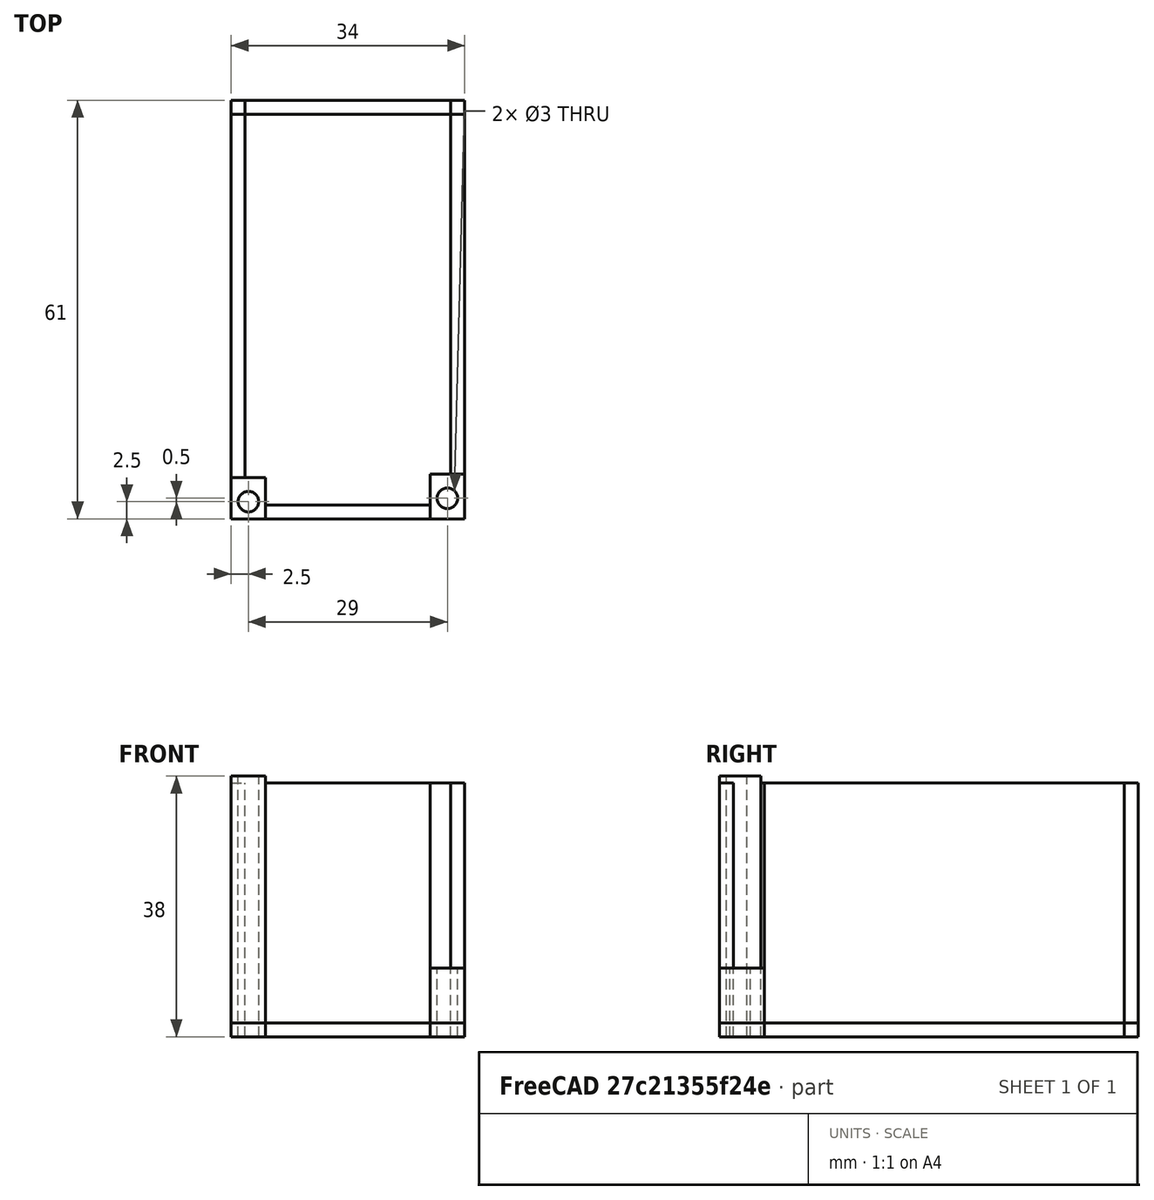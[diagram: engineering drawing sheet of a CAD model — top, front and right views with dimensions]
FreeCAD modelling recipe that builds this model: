
FCSTD DOCUMENT  (FreeCAD 0.16R6700 (Git))
Label: Battery case
License: All rights reserved
LicenseURL: http://en.wikipedia.org/wiki/All_rights_reserved
objects: Part::Box×7, Part::Cylinder×2, Part::Cut×2
note: 11 computed .brp shape members not serialized (recipe doc carries the construction recipe); baked Part::Feature solids carry a one-line shape summary decoded from their .brp

FEATURE [Part::Box] Box  label="Cube"
  Height = 2
  Length = 34
  Width = 61
FEATURE [Part::Box] Box001  label="Cube001"
  Height = 37
  Length = 2
  Placement = pos=(0,6,0) rot=(0,0,1;0rad)
  Width = 55
FEATURE [Part::Box] Box002  label="Cube002"
  Height = 37
  Length = 2
  Placement = pos=(32,6.5,0) rot=(0,0,1;0rad)
  Width = 54.5
FEATURE [Part::Box] Box003  label="Cube003"
  Height = 37
  Length = 34
  Placement = pos=(0,59,0) rot=(0,0,1;0rad)
  Width = 2
FEATURE [Part::Box] Box004  label="Cube004"
  Height = 37
  Length = 24
  Placement = pos=(5,0,0) rot=(0,0,1;0rad)
  Width = 2
FEATURE [Part::Cylinder] Cylinder
  Angle = 360
  Height = 38
  Placement = pos=(2.5,2.5,0) rot=(0,0,1;0rad)
  Radius = 1.5
FEATURE [Part::Box] Box005  label="Cube005"
  Height = 38
  Length = 5
  Width = 6
FEATURE [Part::Box] Box006  label="Cube006"
  Height = 10
  Length = 5
  Placement = pos=(29,0,0) rot=(0,0,1;0rad)
  Width = 6.5
FEATURE [Part::Cylinder] Cylinder001
  Angle = 360
  Height = 10
  Placement = pos=(31.5,3,0) rot=(0,0,1;0rad)
  Radius = 1.5
FEATURE [Part::Cut] Cut
  Base = -> Box006
  Tool = -> Cylinder001
FEATURE [Part::Cut] Cut001
  Base = -> Box005
  Tool = -> Cylinder
